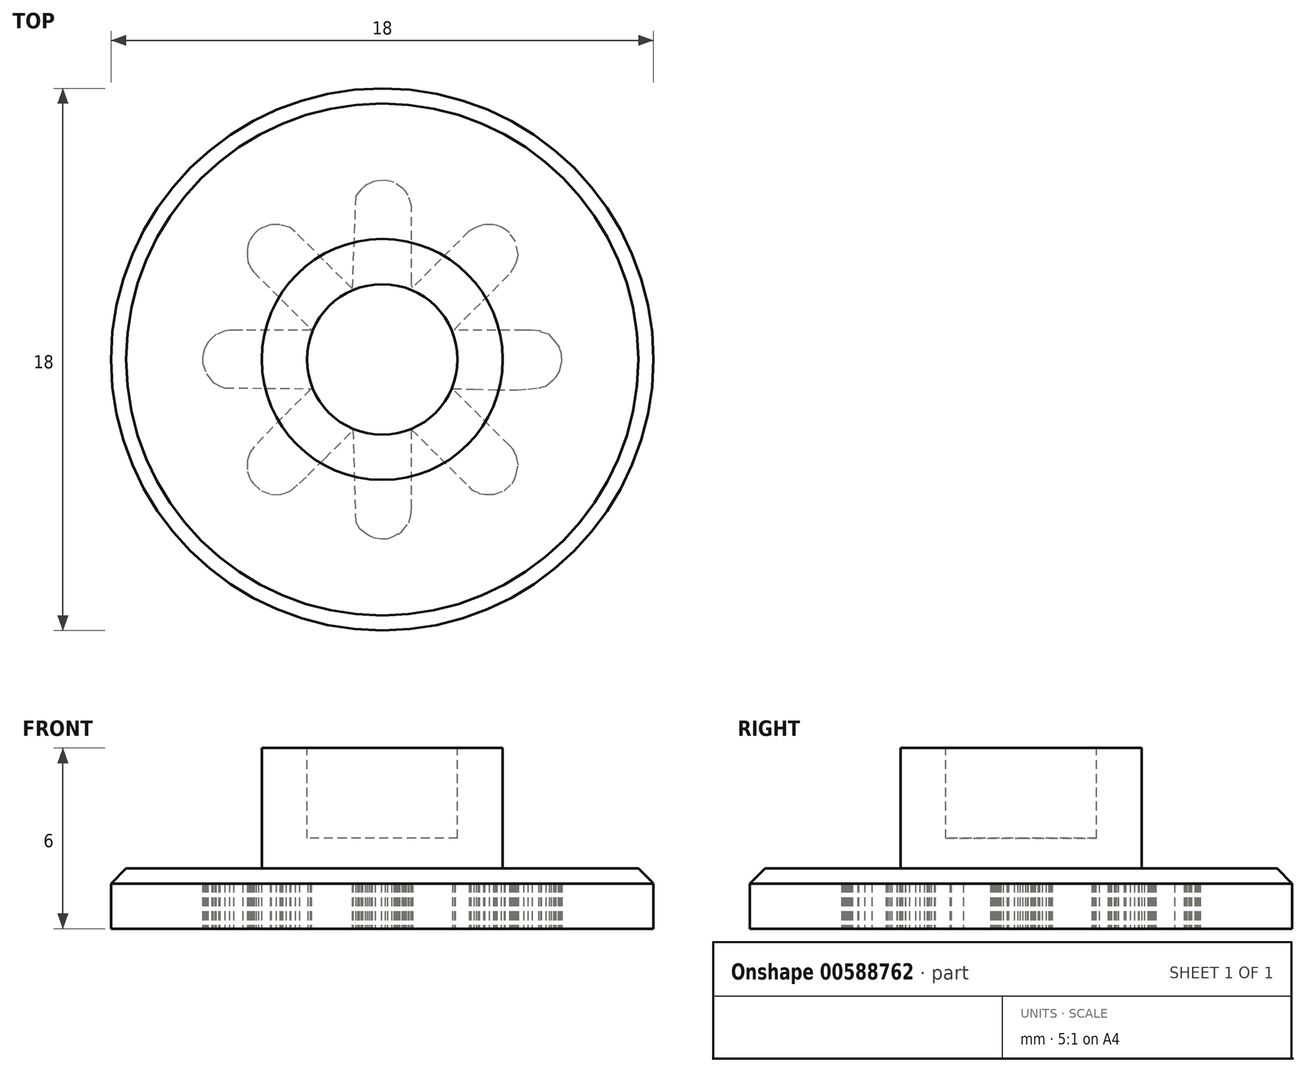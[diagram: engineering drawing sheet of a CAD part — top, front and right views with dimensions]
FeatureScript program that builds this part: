
annotation { "Feature Type Name" : "Feature", "Feature Type Description" : "" }
export const myFeature = defineFeature(function(context is Context, id is Id, definition is map)
    precondition{}
    {
        {
            var Q0;
            Q0=qCreatedBy(makeId("Top.planeOp"),FACE);
            var sketch = newSketch(context, id + "F0", { "sketchPlane" : qUnion([Q0])});
            skCircle(sketch, "E0", {"center": v(0, 0) * mm, "radius": 9 * mm});
            skSolve(sketch);
        }
        {
            var Q0;
            Q0=qSketchRegion(id+"F0",true);
            extrude(context, id + "F1", {"entities" : qUnion([Q0]), "depth" : 2 * mm, "offsetDistance" : 25 * mm});
        }
        {
            var Q0;
            Q0=makeQuery(id+"F1.opExtrude","CAP_FACE",FACE,{"disambiguationData":[OSD([sQuery(id+"F0.wireOp",EDGE,"E0")])],"isStart":false});
            var sketch = newSketch(context, id + "F2", { "sketchPlane" : qUnion([Q0])});
            skCircle(sketch, "E1", {"center": v(0, 0) * mm, "radius": 4 * mm});
            skSolve(sketch);
        }
        {
            var Q0;
            Q0=qSketchRegion(id+"F2",true);
            extrude(context, id + "F3", {"entities" : qUnion([Q0]), "operationType" : NewBodyOperationType.ADD, "depth" : 4 * mm, "offsetDistance" : 25 * mm});
        }
        {
            var Q0;
            Q0=makeQuery(id+"F3.opExtrude","CAP_FACE",FACE,{"disambiguationData":[OSD([sQuery(id+"F2.wireOp",EDGE,"E1")])],"isStart":false});
            var sketch = newSketch(context, id + "F4", { "sketchPlane" : qUnion([Q0])});
            skCircle(sketch, "E2", {"center": v(0, 0) * mm, "radius": 2.5 * mm});
            skSolve(sketch);
        }
        {
            var Q0;
            Q0=qSketchRegion(id+"F4",true);
            extrude(context, id + "F5", {"entities" : qUnion([Q0]), "operationType" : NewBodyOperationType.REMOVE, "oppositeDirection" : true, "depth" : 3 * mm, "offsetDistance" : 25 * mm});
        }
        {
            var Q0;
            Q0=makeQuery(id+"F1.opExtrude","CAP_EDGE",EDGE,{"disambiguationData":[OSD([sQuery(id+"F0.wireOp",EDGE,"E0")])],"isStart":false});
            chamfer(context, id + "F6", {"entities" : qUnion([Q0]), "width" : .5 * mm, "tangentPropagation" : true});
        }
        {
            var Q0;
            Q0=makeQuery(id+"F1.opExtrude","CAP_FACE",FACE,{"disambiguationData":[OSD([sQuery(id+"F0.wireOp",EDGE,"E0")])],"isStart":true});
            var sketch = newSketch(context, id + "F7", { "sketchPlane" : qUnion([Q0])});
            skLineSegment(sketch, "E3", {"start": v(-0.24, 5.92) * mm, "end": v(-0.03, 5.95) * mm});
            skLineSegment(sketch, "E4", {"start": v(-0.03, 5.95) * mm, "end": v(0.18, 5.95) * mm});
            skLineSegment(sketch, "E5", {"start": v(0.18, 5.95) * mm, "end": v(0.31, 5.9) * mm});
            skLineSegment(sketch, "E6", {"start": v(0.31, 5.9) * mm, "end": v(0.44, 5.83) * mm});
            skLineSegment(sketch, "E7", {"start": v(0.44, 5.83) * mm, "end": v(0.47, 5.81) * mm});
            skLineSegment(sketch, "E8", {"start": v(0.47, 5.81) * mm, "end": v(0.5, 5.8) * mm});
            skLineSegment(sketch, "E9", {"start": v(0.5, 5.8) * mm, "end": v(0.54, 5.8) * mm});
            skLineSegment(sketch, "E10", {"start": v(0.54, 5.8) * mm, "end": v(0.58, 5.77) * mm});
            skLineSegment(sketch, "E11", {"start": v(0.58, 5.77) * mm, "end": v(0.65, 5.71) * mm});
            skLineSegment(sketch, "E12", {"start": v(0.65, 5.71) * mm, "end": v(0.89, 5.42) * mm});
            skLineSegment(sketch, "E13", {"start": v(0.89, 5.42) * mm, "end": v(0.95, 5.19) * mm});
            skLineSegment(sketch, "E14", {"start": v(0.95, 5.19) * mm, "end": v(0.97, 4.95) * mm});
            skLineSegment(sketch, "E15", {"start": v(0.97, 4.95) * mm, "end": v(0.97, 3.1) * mm});
            skLineSegment(sketch, "E16", {"start": v(0.97, 3.1) * mm, "end": v(0.97, 2.33) * mm});
            skLineSegment(sketch, "E17", {"start": v(0.97, 2.33) * mm, "end": v(1.92, 3.27) * mm});
            skLineSegment(sketch, "E18", {"start": v(1.92, 3.27) * mm, "end": v(2.86, 4.21) * mm});
            skLineSegment(sketch, "E19", {"start": v(2.86, 4.21) * mm, "end": v(2.94, 4.3) * mm});
            skLineSegment(sketch, "E20", {"start": v(2.94, 4.3) * mm, "end": v(3.04, 4.36) * mm});
            skLineSegment(sketch, "E21", {"start": v(3.04, 4.36) * mm, "end": v(3.19, 4.42) * mm});
            skLineSegment(sketch, "E22", {"start": v(3.19, 4.42) * mm, "end": v(3.22, 4.45) * mm});
            skLineSegment(sketch, "E23", {"start": v(3.22, 4.45) * mm, "end": v(3.4, 4.48) * mm});
            skLineSegment(sketch, "E24", {"start": v(3.4, 4.48) * mm, "end": v(3.56, 4.48) * mm});
            skLineSegment(sketch, "E25", {"start": v(3.56, 4.48) * mm, "end": v(3.72, 4.48) * mm});
            skLineSegment(sketch, "E26", {"start": v(3.72, 4.48) * mm, "end": v(4.04, 4.36) * mm});
            skLineSegment(sketch, "E27", {"start": v(4.04, 4.36) * mm, "end": v(4.3, 4.12) * mm});
            skLineSegment(sketch, "E28", {"start": v(4.3, 4.12) * mm, "end": v(4.39, 3.98) * mm});
            skLineSegment(sketch, "E29", {"start": v(4.39, 3.98) * mm, "end": v(4.44, 3.83) * mm});
            skLineSegment(sketch, "E30", {"start": v(4.44, 3.83) * mm, "end": v(4.51, 3.5) * mm});
            skLineSegment(sketch, "E31", {"start": v(4.51, 3.5) * mm, "end": v(4.45, 3.2) * mm});
            skLineSegment(sketch, "E32", {"start": v(4.45, 3.2) * mm, "end": v(4.4, 3.12) * mm});
            skLineSegment(sketch, "E33", {"start": v(4.4, 3.12) * mm, "end": v(4.38, 3.05) * mm});
            skLineSegment(sketch, "E34", {"start": v(4.38, 3.05) * mm, "end": v(4.34, 2.98) * mm});
            skLineSegment(sketch, "E35", {"start": v(4.34, 2.98) * mm, "end": v(4.22, 2.86) * mm});
            skLineSegment(sketch, "E36", {"start": v(4.22, 2.86) * mm, "end": v(3.27, 1.91) * mm});
            skLineSegment(sketch, "E37", {"start": v(3.27, 1.91) * mm, "end": v(2.33, 0.97) * mm});
            skLineSegment(sketch, "E38", {"start": v(2.33, 0.97) * mm, "end": v(3.05, 0.98) * mm});
            skLineSegment(sketch, "E39", {"start": v(3.05, 0.98) * mm, "end": v(3.77, 1.01) * mm});
            skLineSegment(sketch, "E40", {"start": v(3.77, 1.01) * mm, "end": v(4.48, 1.01) * mm});
            skLineSegment(sketch, "E41", {"start": v(4.48, 1.01) * mm, "end": v(4.84, 0.99) * mm});
            skLineSegment(sketch, "E42", {"start": v(4.84, 0.99) * mm, "end": v(5.2, 0.94) * mm});
            skLineSegment(sketch, "E43", {"start": v(5.2, 0.94) * mm, "end": v(5.43, 0.88) * mm});
            skLineSegment(sketch, "E44", {"start": v(5.43, 0.88) * mm, "end": v(5.6, 0.74) * mm});
            skLineSegment(sketch, "E45", {"start": v(5.6, 0.74) * mm, "end": v(5.69, 0.67) * mm});
            skLineSegment(sketch, "E46", {"start": v(5.69, 0.67) * mm, "end": v(5.76, 0.6) * mm});
            skLineSegment(sketch, "E47", {"start": v(5.76, 0.6) * mm, "end": v(5.87, 0.41) * mm});
            skLineSegment(sketch, "E48", {"start": v(5.87, 0.41) * mm, "end": v(5.93, 0.23) * mm});
            skLineSegment(sketch, "E49", {"start": v(5.93, 0.23) * mm, "end": v(5.96, 0.04) * mm});
            skLineSegment(sketch, "E50", {"start": v(5.96, 0.04) * mm, "end": v(5.95, -0.15) * mm});
            skLineSegment(sketch, "E51", {"start": v(5.95, -0.15) * mm, "end": v(5.93, -0.24) * mm});
            skLineSegment(sketch, "E52", {"start": v(5.93, -0.24) * mm, "end": v(5.9, -0.32) * mm});
            skLineSegment(sketch, "E53", {"start": v(5.9, -0.32) * mm, "end": v(5.88, -0.4) * mm});
            skLineSegment(sketch, "E54", {"start": v(5.88, -0.4) * mm, "end": v(5.84, -0.48) * mm});
            skLineSegment(sketch, "E55", {"start": v(5.84, -0.48) * mm, "end": v(5.72, -0.62) * mm});
            skLineSegment(sketch, "E56", {"start": v(5.72, -0.62) * mm, "end": v(5.55, -0.82) * mm});
            skLineSegment(sketch, "E57", {"start": v(5.55, -0.82) * mm, "end": v(5.28, -0.91) * mm});
            skLineSegment(sketch, "E58", {"start": v(5.28, -0.91) * mm, "end": v(5.25, -0.94) * mm});
            skLineSegment(sketch, "E59", {"start": v(5.25, -0.94) * mm, "end": v(4.97, -0.97) * mm});
            skLineSegment(sketch, "E60", {"start": v(4.97, -0.97) * mm, "end": v(4.7, -0.97) * mm});
            skLineSegment(sketch, "E61", {"start": v(4.7, -0.97) * mm, "end": v(2.86, -0.97) * mm});
            skLineSegment(sketch, "E62", {"start": v(2.86, -0.97) * mm, "end": v(2.42, -0.97) * mm});
            skLineSegment(sketch, "E63", {"start": v(2.42, -0.97) * mm, "end": v(2.4, -1) * mm});
            skLineSegment(sketch, "E64", {"start": v(2.4, -1) * mm, "end": v(3.33, -1.94) * mm});
            skLineSegment(sketch, "E65", {"start": v(3.33, -1.94) * mm, "end": v(4.28, -2.89) * mm});
            skLineSegment(sketch, "E66", {"start": v(4.28, -2.89) * mm, "end": v(4.3, -2.95) * mm});
            skLineSegment(sketch, "E67", {"start": v(4.3, -2.95) * mm, "end": v(4.34, -3) * mm});
            skLineSegment(sketch, "E68", {"start": v(4.34, -3) * mm, "end": v(4.4, -3.11) * mm});
            skLineSegment(sketch, "E69", {"start": v(4.4, -3.11) * mm, "end": v(4.44, -3.23) * mm});
            skLineSegment(sketch, "E70", {"start": v(4.44, -3.23) * mm, "end": v(4.51, -3.47) * mm});
            skLineSegment(sketch, "E71", {"start": v(4.51, -3.47) * mm, "end": v(4.43, -3.92) * mm});
            skLineSegment(sketch, "E72", {"start": v(4.43, -3.92) * mm, "end": v(4.22, -4.21) * mm});
            skLineSegment(sketch, "E73", {"start": v(4.22, -4.21) * mm, "end": v(4.07, -4.33) * mm});
            skLineSegment(sketch, "E74", {"start": v(4.07, -4.33) * mm, "end": v(3.94, -4.4) * mm});
            skLineSegment(sketch, "E75", {"start": v(3.94, -4.4) * mm, "end": v(3.8, -4.45) * mm});
            skLineSegment(sketch, "E76", {"start": v(3.8, -4.45) * mm, "end": v(3.69, -4.48) * mm});
            skLineSegment(sketch, "E77", {"start": v(3.69, -4.48) * mm, "end": v(3.36, -4.48) * mm});
            skLineSegment(sketch, "E78", {"start": v(3.36, -4.48) * mm, "end": v(3.12, -4.39) * mm});
            skLineSegment(sketch, "E79", {"start": v(3.12, -4.39) * mm, "end": v(2.9, -4.27) * mm});
            skLineSegment(sketch, "E80", {"start": v(2.9, -4.27) * mm, "end": v(1.95, -3.33) * mm});
            skLineSegment(sketch, "E81", {"start": v(1.95, -3.33) * mm, "end": v(1, -2.39) * mm});
            skLineSegment(sketch, "E82", {"start": v(1, -2.39) * mm, "end": v(0.98, -2.43) * mm});
            skLineSegment(sketch, "E83", {"start": v(0.98, -2.43) * mm, "end": v(0.97, -2.48) * mm});
            skLineSegment(sketch, "E84", {"start": v(0.97, -2.48) * mm, "end": v(0.97, -2.6) * mm});
            skLineSegment(sketch, "E85", {"start": v(0.97, -2.6) * mm, "end": v(0.97, -4.42) * mm});
            skLineSegment(sketch, "E86", {"start": v(0.97, -4.42) * mm, "end": v(0.97, -5.1) * mm});
            skLineSegment(sketch, "E87", {"start": v(0.97, -5.1) * mm, "end": v(0.86, -5.45) * mm});
            skLineSegment(sketch, "E88", {"start": v(0.86, -5.45) * mm, "end": v(0.8, -5.56) * mm});
            skLineSegment(sketch, "E89", {"start": v(0.8, -5.56) * mm, "end": v(0.75, -5.61) * mm});
            skLineSegment(sketch, "E90", {"start": v(0.75, -5.61) * mm, "end": v(0.7, -5.65) * mm});
            skLineSegment(sketch, "E91", {"start": v(0.7, -5.65) * mm, "end": v(0.38, -5.89) * mm});
            skLineSegment(sketch, "E92", {"start": v(0.38, -5.89) * mm, "end": v(0.09, -5.95) * mm});
            skLineSegment(sketch, "E93", {"start": v(0.09, -5.95) * mm, "end": v(-0.24, -5.92) * mm});
            skLineSegment(sketch, "E94", {"start": v(-0.24, -5.92) * mm, "end": v(-0.34, -5.89) * mm});
            skLineSegment(sketch, "E95", {"start": v(-0.34, -5.89) * mm, "end": v(-0.44, -5.83) * mm});
            skLineSegment(sketch, "E96", {"start": v(-0.44, -5.83) * mm, "end": v(-0.5, -5.8) * mm});
            skLineSegment(sketch, "E97", {"start": v(-0.5, -5.8) * mm, "end": v(-0.56, -5.77) * mm});
            skLineSegment(sketch, "E98", {"start": v(-0.56, -5.77) * mm, "end": v(-0.7, -5.65) * mm});
            skLineSegment(sketch, "E99", {"start": v(-0.7, -5.65) * mm, "end": v(-0.83, -5.5) * mm});
            skLineSegment(sketch, "E100", {"start": v(-0.83, -5.5) * mm, "end": v(-0.88, -5.42) * mm});
            skLineSegment(sketch, "E101", {"start": v(-0.88, -5.42) * mm, "end": v(-1, -2.36) * mm});
            skLineSegment(sketch, "E102", {"start": v(-1, -2.36) * mm, "end": v(-1.95, -3.3) * mm});
            skLineSegment(sketch, "E103", {"start": v(-1.95, -3.3) * mm, "end": v(-2.9, -4.24) * mm});
            skLineSegment(sketch, "E104", {"start": v(-2.9, -4.24) * mm, "end": v(-3.07, -4.39) * mm});
            skLineSegment(sketch, "E105", {"start": v(-3.07, -4.39) * mm, "end": v(-3.4, -4.48) * mm});
            skLineSegment(sketch, "E106", {"start": v(-3.4, -4.48) * mm, "end": v(-3.72, -4.48) * mm});
            skLineSegment(sketch, "E107", {"start": v(-3.72, -4.48) * mm, "end": v(-4.01, -4.36) * mm});
            skLineSegment(sketch, "E108", {"start": v(-4.01, -4.36) * mm, "end": v(-4.1, -4.3) * mm});
            skLineSegment(sketch, "E109", {"start": v(-4.1, -4.3) * mm, "end": v(-4.19, -4.24) * mm});
            skLineSegment(sketch, "E110", {"start": v(-4.19, -4.24) * mm, "end": v(-4.3, -4.1) * mm});
            skLineSegment(sketch, "E111", {"start": v(-4.3, -4.1) * mm, "end": v(-4.37, -4) * mm});
            skLineSegment(sketch, "E112", {"start": v(-4.37, -4) * mm, "end": v(-4.42, -3.89) * mm});
            skLineSegment(sketch, "E113", {"start": v(-4.42, -3.89) * mm, "end": v(-4.46, -3.76) * mm});
            skLineSegment(sketch, "E114", {"start": v(-4.46, -3.76) * mm, "end": v(-4.48, -3.62) * mm});
            skLineSegment(sketch, "E115", {"start": v(-4.48, -3.62) * mm, "end": v(-4.48, -3.42) * mm});
            skLineSegment(sketch, "E116", {"start": v(-4.48, -3.42) * mm, "end": v(-4.45, -3.2) * mm});
            skLineSegment(sketch, "E117", {"start": v(-4.45, -3.2) * mm, "end": v(-4.42, -3.16) * mm});
            skLineSegment(sketch, "E118", {"start": v(-4.42, -3.16) * mm, "end": v(-4.4, -3.1) * mm});
            skLineSegment(sketch, "E119", {"start": v(-4.4, -3.1) * mm, "end": v(-4.34, -3) * mm});
            skLineSegment(sketch, "E120", {"start": v(-4.34, -3) * mm, "end": v(-4.28, -2.92) * mm});
            skLineSegment(sketch, "E121", {"start": v(-4.28, -2.92) * mm, "end": v(-3.33, -1.97) * mm});
            skLineSegment(sketch, "E122", {"start": v(-3.33, -1.97) * mm, "end": v(-2.39, -1.03) * mm});
            skLineSegment(sketch, "E123", {"start": v(-2.39, -1.03) * mm, "end": v(-2.37, -1) * mm});
            skLineSegment(sketch, "E124", {"start": v(-2.37, -1) * mm, "end": v(-2.36, -0.97) * mm});
            skLineSegment(sketch, "E125", {"start": v(-2.36, -0.97) * mm, "end": v(-4.19, -0.97) * mm});
            skLineSegment(sketch, "E126", {"start": v(-4.19, -0.97) * mm, "end": v(-4.63, -0.97) * mm});
            skLineSegment(sketch, "E127", {"start": v(-4.63, -0.97) * mm, "end": v(-4.93, -0.98) * mm});
            skLineSegment(sketch, "E128", {"start": v(-4.93, -0.98) * mm, "end": v(-5.08, -0.97) * mm});
            skLineSegment(sketch, "E129", {"start": v(-5.08, -0.97) * mm, "end": v(-5.22, -0.94) * mm});
            skLineSegment(sketch, "E130", {"start": v(-5.22, -0.94) * mm, "end": v(-5.52, -0.82) * mm});
            skLineSegment(sketch, "E131", {"start": v(-5.52, -0.82) * mm, "end": v(-5.66, -0.7) * mm});
            skLineSegment(sketch, "E132", {"start": v(-5.66, -0.7) * mm, "end": v(-5.78, -0.56) * mm});
            skLineSegment(sketch, "E133", {"start": v(-5.78, -0.56) * mm, "end": v(-5.84, -0.46) * mm});
            skLineSegment(sketch, "E134", {"start": v(-5.84, -0.46) * mm, "end": v(-5.9, -0.35) * mm});
            skLineSegment(sketch, "E135", {"start": v(-5.9, -0.35) * mm, "end": v(-5.94, -0.2) * mm});
            skLineSegment(sketch, "E136", {"start": v(-5.94, -0.2) * mm, "end": v(-5.96, -0.06) * mm});
            skLineSegment(sketch, "E137", {"start": v(-5.96, -0.06) * mm, "end": v(-5.96, 0.12) * mm});
            skLineSegment(sketch, "E138", {"start": v(-5.96, 0.12) * mm, "end": v(-5.84, 0.47) * mm});
            skLineSegment(sketch, "E139", {"start": v(-5.84, 0.47) * mm, "end": v(-5.66, 0.7) * mm});
            skLineSegment(sketch, "E140", {"start": v(-5.66, 0.7) * mm, "end": v(-5.61, 0.76) * mm});
            skLineSegment(sketch, "E141", {"start": v(-5.61, 0.76) * mm, "end": v(-5.56, 0.8) * mm});
            skLineSegment(sketch, "E142", {"start": v(-5.56, 0.8) * mm, "end": v(-5.43, 0.85) * mm});
            skLineSegment(sketch, "E143", {"start": v(-5.43, 0.85) * mm, "end": v(-5.4, 0.88) * mm});
            skLineSegment(sketch, "E144", {"start": v(-5.4, 0.88) * mm, "end": v(-5.22, 0.94) * mm});
            skLineSegment(sketch, "E145", {"start": v(-5.22, 0.94) * mm, "end": v(-2.36, 0.97) * mm});
            skLineSegment(sketch, "E146", {"start": v(-2.36, 0.97) * mm, "end": v(-3.3, 1.91) * mm});
            skLineSegment(sketch, "E147", {"start": v(-3.3, 1.91) * mm, "end": v(-4.25, 2.89) * mm});
            skLineSegment(sketch, "E148", {"start": v(-4.25, 2.89) * mm, "end": v(-4.4, 3.1) * mm});
            skLineSegment(sketch, "E149", {"start": v(-4.4, 3.1) * mm, "end": v(-4.48, 3.36) * mm});
            skLineSegment(sketch, "E150", {"start": v(-4.48, 3.36) * mm, "end": v(-4.48, 3.71) * mm});
            skLineSegment(sketch, "E151", {"start": v(-4.48, 3.71) * mm, "end": v(-4.4, 3.93) * mm});
            skLineSegment(sketch, "E152", {"start": v(-4.4, 3.93) * mm, "end": v(-4.35, 4.03) * mm});
            skLineSegment(sketch, "E153", {"start": v(-4.35, 4.03) * mm, "end": v(-4.28, 4.12) * mm});
            skLineSegment(sketch, "E154", {"start": v(-4.28, 4.12) * mm, "end": v(-4.01, 4.36) * mm});
            skLineSegment(sketch, "E155", {"start": v(-4.01, 4.36) * mm, "end": v(-3.69, 4.48) * mm});
            skLineSegment(sketch, "E156", {"start": v(-3.69, 4.48) * mm, "end": v(-3.52, 4.49) * mm});
            skLineSegment(sketch, "E157", {"start": v(-3.52, 4.49) * mm, "end": v(-3.36, 4.48) * mm});
            skLineSegment(sketch, "E158", {"start": v(-3.36, 4.48) * mm, "end": v(-3.2, 4.42) * mm});
            skLineSegment(sketch, "E159", {"start": v(-3.2, 4.42) * mm, "end": v(-3.04, 4.36) * mm});
            skLineSegment(sketch, "E160", {"start": v(-3.04, 4.36) * mm, "end": v(-2.75, 4.1) * mm});
            skLineSegment(sketch, "E161", {"start": v(-2.75, 4.1) * mm, "end": v(-2.46, 3.84) * mm});
            skLineSegment(sketch, "E162", {"start": v(-2.46, 3.84) * mm, "end": v(-1.92, 3.3) * mm});
            skLineSegment(sketch, "E163", {"start": v(-1.92, 3.3) * mm, "end": v(-0.97, 2.36) * mm});
            skLineSegment(sketch, "E164", {"start": v(-0.97, 2.36) * mm, "end": v(-0.88, 5.39) * mm});
            skLineSegment(sketch, "E165", {"start": v(-0.88, 5.39) * mm, "end": v(-0.77, 5.6) * mm});
            skLineSegment(sketch, "E166", {"start": v(-0.77, 5.6) * mm, "end": v(-0.71, 5.64) * mm});
            skLineSegment(sketch, "E167", {"start": v(-0.71, 5.64) * mm, "end": v(-0.65, 5.68) * mm});
            skLineSegment(sketch, "E168", {"start": v(-0.65, 5.68) * mm, "end": v(-0.5, 5.8) * mm});
            skLineSegment(sketch, "E169", {"start": v(-0.5, 5.8) * mm, "end": v(-0.37, 5.87) * mm});
            skLineSegment(sketch, "E170", {"start": v(-0.37, 5.87) * mm, "end": v(-0.24, 5.92) * mm});
            skSolve(sketch);
        }
        {
            var Q0;
            Q0 = qSketchRegion(id + "F7", true);
            extrude(context, id + "F8", {"entities" : qUnion([Q0]), "operationType" : NewBodyOperationType.REMOVE, "oppositeDirection" : true, "depth" : 1.5 * mm, "offsetDistance" : 25 * mm});
        }
    });
